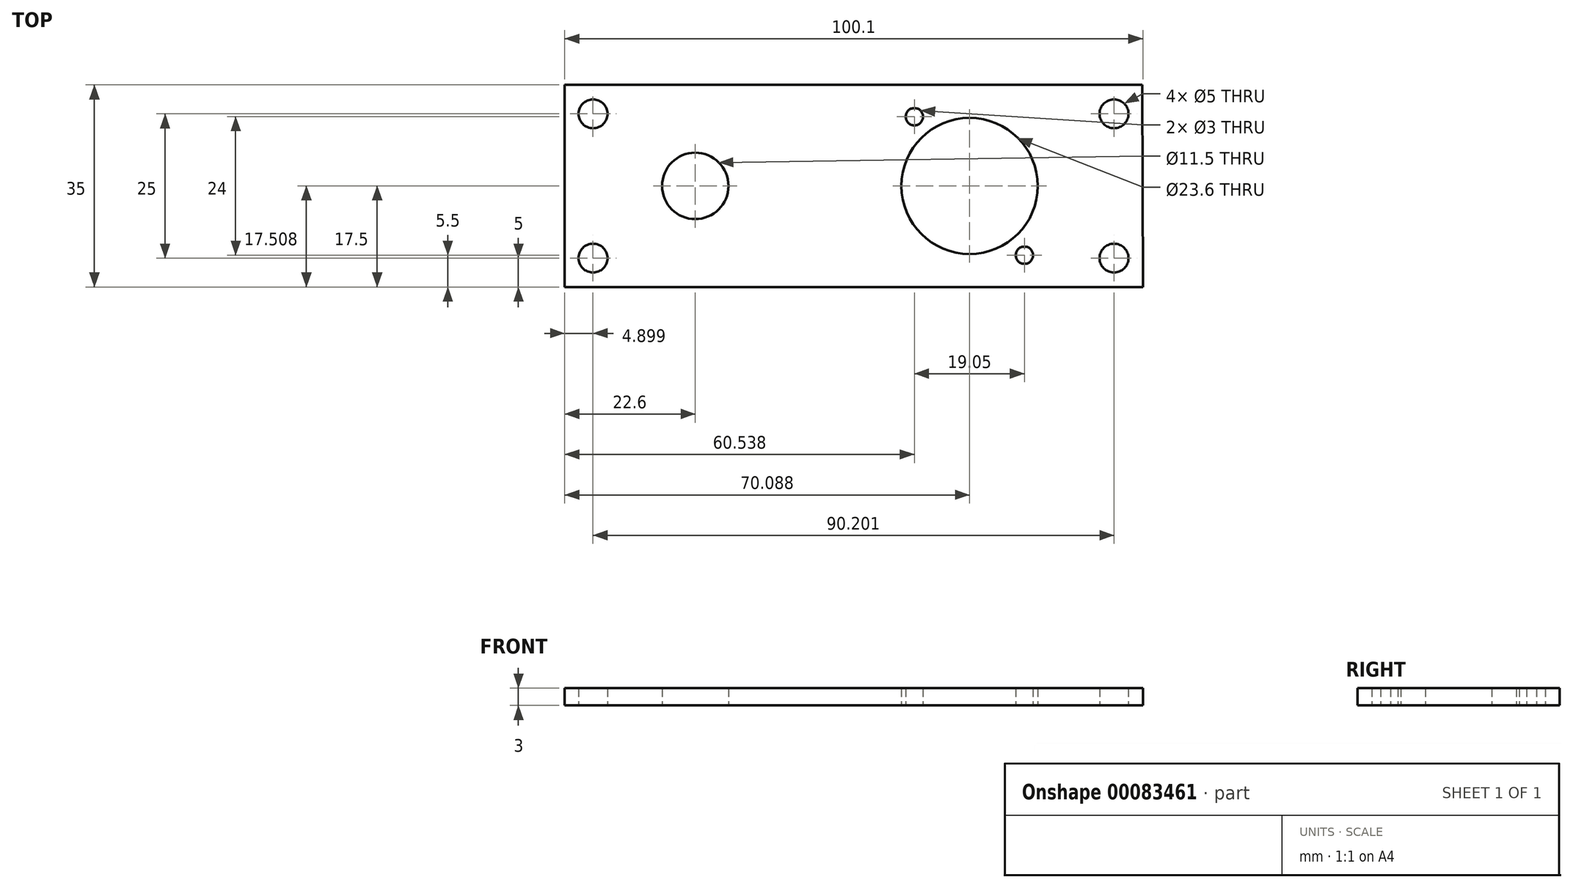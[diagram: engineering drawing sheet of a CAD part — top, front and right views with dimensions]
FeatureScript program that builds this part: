
annotation { "Feature Type Name" : "Feature", "Feature Type Description" : "" }
export const myFeature = defineFeature(function(context is Context, id is Id, definition is map)
    precondition{}
    {
        {
            var Q0;
            Q0=qCreatedBy(makeId("Top.planeOp"),FACE);
            var sketch = newSketch(context, id + "F0", { "sketchPlane" : qUnion([Q0])});
            skLineSegment(sketch, "E0.bottom", {"start": v(0, 35) * mm, "end": v(100, 35) * mm});
            skLineSegment(sketch, "E0.top", {"start": v(0, 0) * mm, "end": v(100.1, 0) * mm});
            skLineSegment(sketch, "E0.right", {"start": v(100, 35) * mm, "end": v(100.1, 0) * mm});
            skCircle(sketch, "E1", {"center": v(70.09, 17.5) * mm, "radius": 11.8 * mm});
            skCircle(sketch, "E2", {"center": v(22.6, 17.5) * mm, "radius": 5.75 * mm});
            skLineSegment(sketch, "E3", {"start": v(0, 35) * mm, "end": v(0, 0) * mm});
            skCircle(sketch, "E4", {"center": v(60.54, 29.5) * mm, "radius": 1.5 * mm});
            skCircle(sketch, "E5", {"center": v(79.59, 5.5) * mm, "radius": 1.5 * mm});
            skCircle(sketch, "E6", {"center": v(95.1, 5) * mm, "radius": 2.5 * mm});
            skCircle(sketch, "E7.MirrorC", {"center": v(95.1, 30) * mm, "radius": 2.5 * mm});
            skCircle(sketch, "E8.MirrorC", {"center": v(4.9, 30) * mm, "radius": 2.5 * mm});
            skCircle(sketch, "E9.MirrorC", {"center": v(4.9, 5) * mm, "radius": 2.5 * mm});
            skSolve(sketch);
        }
        {
            var Q0;
            Q0=makeQuery(id+"F0.imprint","IMPRINT",FACE,{"disambiguationData":[TD([[makeQuery(id+"F0.imprint","IMPRINT",EDGE,{"derivedFrom":sQuery(id+"F0.wireOp",EDGE,"E0.bottom")}),-1.0]])]});
            extrude(context, id + "F1", {"entities" : qUnion([Q0]), "depth" : 3 * mm, "offsetDistance" : 25 * mm});
        }
    });
